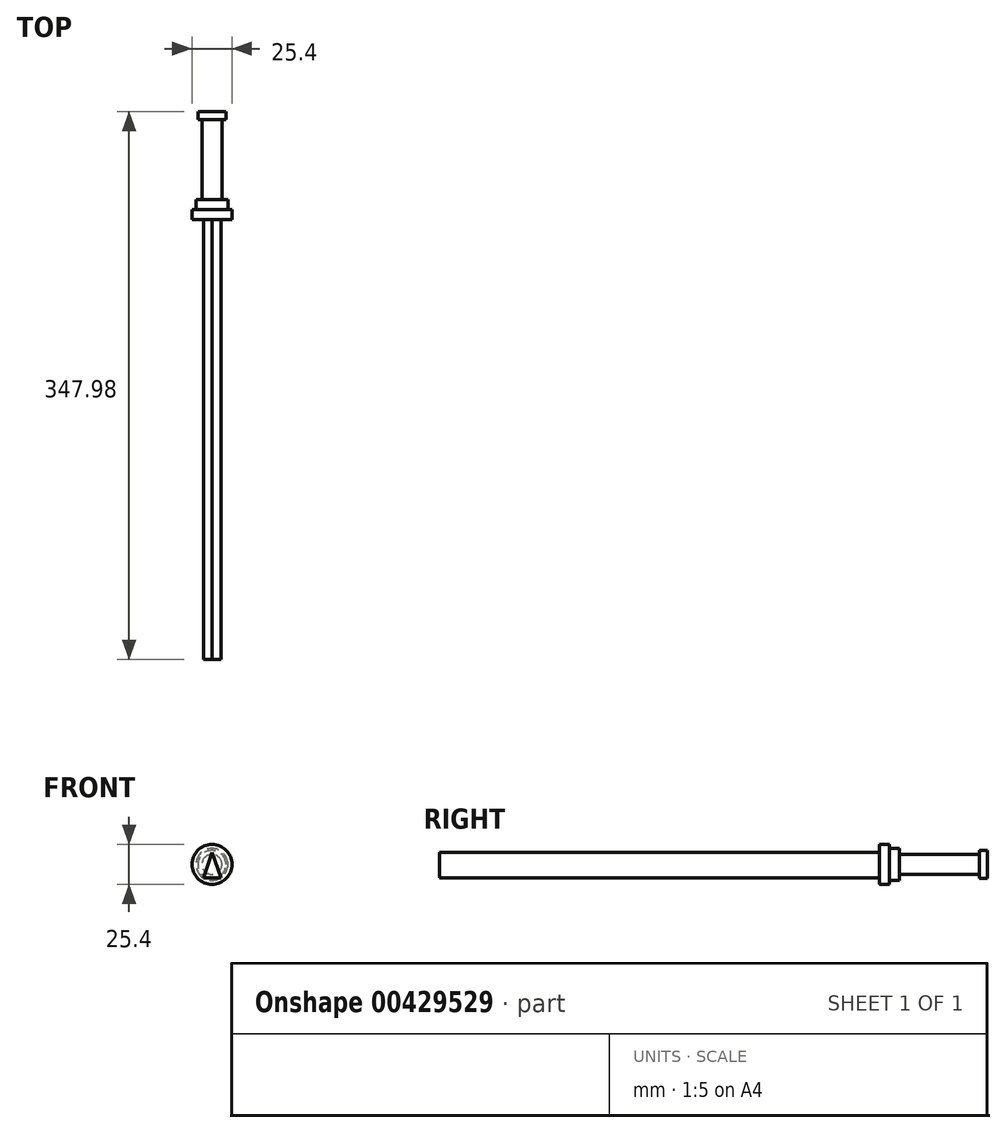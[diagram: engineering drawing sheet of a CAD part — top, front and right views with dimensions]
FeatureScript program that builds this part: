
annotation { "Feature Type Name" : "Feature", "Feature Type Description" : "" }
export const myFeature = defineFeature(function(context is Context, id is Id, definition is map)
    precondition{}
    {
        {
            var Q0;
            Q0=qCreatedBy(makeId("Front.planeOp"),FACE);
            var sketch = newSketch(context, id + "F0", { "sketchPlane" : qUnion([Q0])});
            skCircle(sketch, "E0", {"center": v(-96.86, 20.27) * mm, "radius": 12.7 * mm});
            skSolve(sketch);
        }
        {
            var Q0;
            Q0 = qSketchRegion(id + "F0", true);
            extrude(context, id + "F1", {"entities" : qUnion([Q0]), "oppositeDirection" : true, "depth" : 6.35 * mm});
        }
        {
            var Q0;
            Q0=makeQuery(id+"F1.opExtrude","CAP_FACE",FACE,{"disambiguationData":[OSD([sQuery(id+"F0.wireOp",EDGE,"E0")])],"isStart":false});
            var sketch = newSketch(context, id + "F2", { "sketchPlane" : qUnion([Q0])});
            skCircle(sketch, "E1", {"center": v(96.86, 20.27) * mm, "radius": 10.16 * mm});
            skSolve(sketch);
        }
        {
            var Q0;
            Q0 = qSketchRegion(id + "F2", true);
            extrude(context, id + "F3", {"entities" : qUnion([Q0]), "operationType" : NewBodyOperationType.ADD, "depth" : 6.35 * mm});
        }
        {
            var Q0;
            Q0=makeQuery(id+"F3.opExtrude","CAP_FACE",FACE,{"disambiguationData":[OSD([sQuery(id+"F2.wireOp",EDGE,"E1")])],"isStart":false});
            var sketch = newSketch(context, id + "F4", { "sketchPlane" : qUnion([Q0])});
            skCircle(sketch, "E2", {"center": v(96.86, 20.27) * mm, "radius": 6.35 * mm});
            skSolve(sketch);
        }
        {
            var Q0;
            Q0 = qSketchRegion(id + "F4", true);
            extrude(context, id + "F5", {"entities" : qUnion([Q0]), "operationType" : NewBodyOperationType.ADD, "depth" : 50.8 * mm});
        }
        {
            var Q0;
            Q0=makeQuery(id+"F5.opExtrude","CAP_FACE",FACE,{"disambiguationData":[OSD([sQuery(id+"F4.wireOp",EDGE,"E2")])],"isStart":false});
            var sketch = newSketch(context, id + "F6", { "sketchPlane" : qUnion([Q0])});
            skCircle(sketch, "E3", {"center": v(96.86, 20.27) * mm, "radius": 8.9 * mm});
            skSolve(sketch);
        }
        {
            var Q0;
            Q0 = qSketchRegion(id + "F6", true);
            extrude(context, id + "F7", {"entities" : qUnion([Q0]), "operationType" : NewBodyOperationType.ADD, "depth" : 5.08 * mm});
        }
        {
            var Q0;
            Q0=makeQuery(id+"F0.imprint","IMPRINT",FACE,{"disambiguationData":[TD([[makeQuery(id+"F0.imprint","IMPRINT",EDGE,{"derivedFrom":sQuery(id+"F0.wireOp",EDGE,"E0")}),1.0]])]});
            var sketch = newSketch(context, id + "F8", { "sketchPlane" : qUnion([Q0])});
            skLineSegment(sketch, "E4", {"start": v(-102.12, 11.78) * mm, "end": v(-96.66, 28.01) * mm});
            skLineSegment(sketch, "E5", {"start": v(-96.66, 28.01) * mm, "end": v(-91.16, 11.78) * mm});
            skLineSegment(sketch, "E6", {"start": v(-91.16, 11.78) * mm, "end": v(-102.12, 11.78) * mm});
            skSolve(sketch);
        }
        {
            var Q0;
            Q0 = qSketchRegion(id + "F8", true);
            extrude(context, id + "F9", {"entities" : qUnion([Q0]), "operationType" : NewBodyOperationType.ADD, "depth" : 279.4 * mm});
        }
    });
